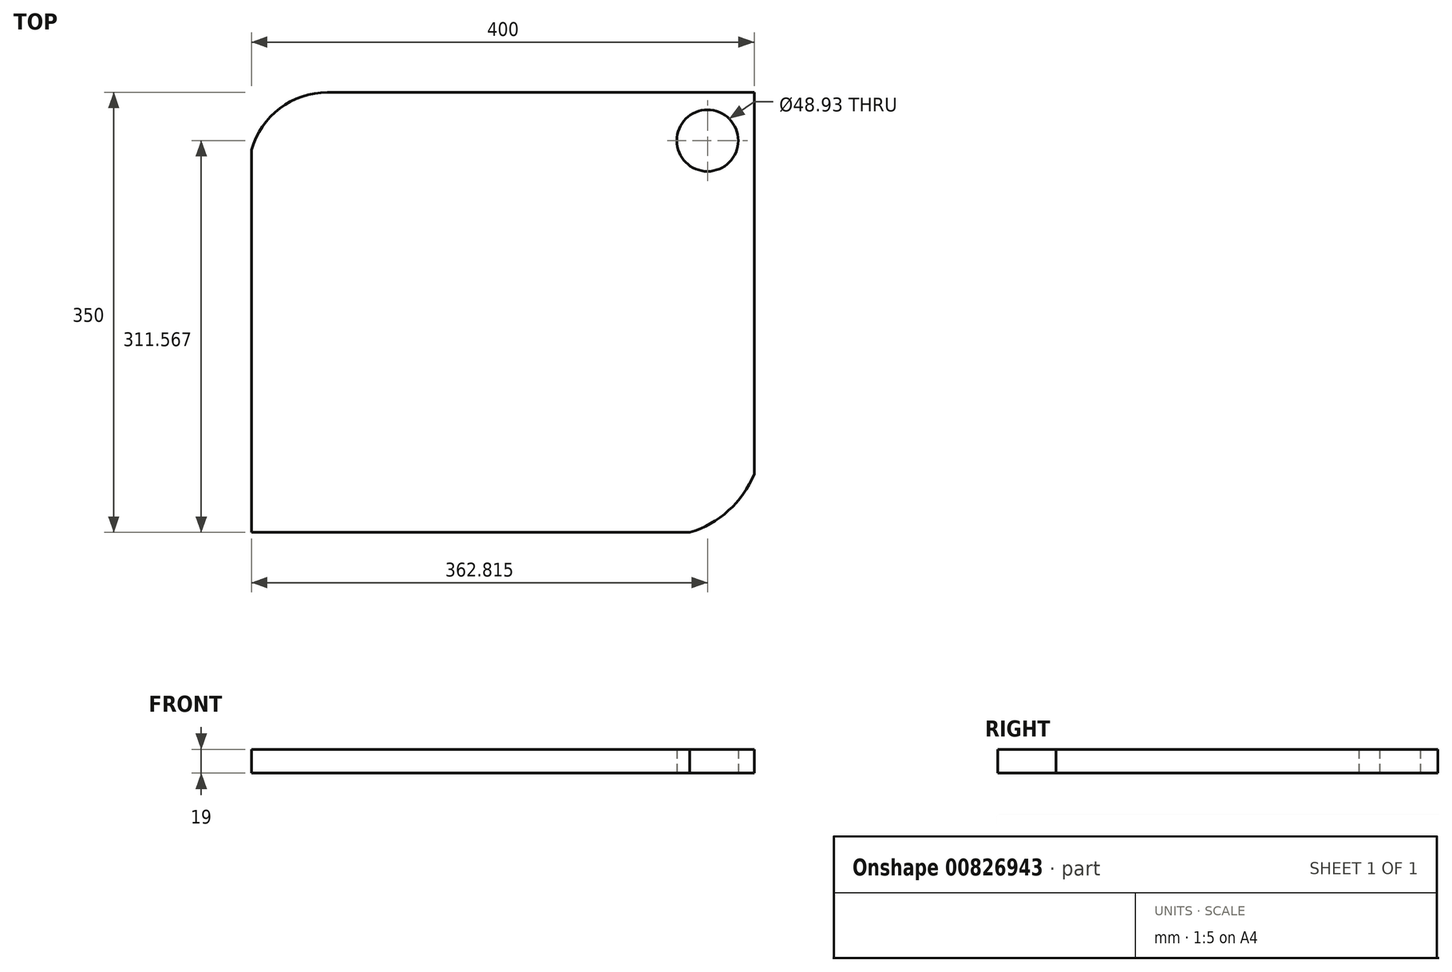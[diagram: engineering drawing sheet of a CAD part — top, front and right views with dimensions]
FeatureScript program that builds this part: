
annotation { "Feature Type Name" : "Feature", "Feature Type Description" : "" }
export const myFeature = defineFeature(function(context is Context, id is Id, definition is map)
    precondition{}
    {
        {
            var Q0;
            Q0=qCreatedBy(makeId("Top.planeOp"),FACE);
            var sketch = newSketch(context, id + "F0", { "sketchPlane" : qUnion([Q0])});
            skLineSegment(sketch, "E0.bottom", {"start": v(200, -175) * mm, "end": v(-200, -175) * mm});
            skLineSegment(sketch, "E0.top", {"start": v(200, 175) * mm, "end": v(-200, 175) * mm});
            skLineSegment(sketch, "E0.left", {"start": v(200, -175) * mm, "end": v(200, 175) * mm});
            skLineSegment(sketch, "E0.right", {"start": v(-200, -175) * mm, "end": v(-200, 175) * mm});
            skPoint(sketch, "E0.middle", {"position": v(0, 0) * mm});
            skSolve(sketch);
        }
        {
            var Q0;
            Q0=qSketchRegion(id+"F0",true);
            extrude(context, id + "F1", {"entities" : qUnion([Q0]), "depth" : 19 * mm, "offsetDistance" : 25 * mm});
        }
        {
            var Q0;
            Q0=makeQuery(id+"F1.opExtrude","CAP_FACE",FACE,{"disambiguationData":[OSD([sQuery(id+"F0.wireOp",EDGE,"E0.bottom"),sQuery(id+"F0.wireOp",EDGE,"E0.top"),sQuery(id+"F0.wireOp",EDGE,"E0.left"),sQuery(id+"F0.wireOp",EDGE,"E0.right")])],"isStart":false});
            var sketch = newSketch(context, id + "F2", { "sketchPlane" : qUnion([Q0])});
            skArc(sketch, "E1", {"start": v(-139.55, 175) * mm, "mid": v(-177.47, 162.18) * mm, "end": v(-200, 129.1) * mm});
            skSolve(sketch);
        }
        {
            var Q0;
            Q0 = qSketchRegion(id + "F2", true);
            var Q1;
            {var subQ0=sQuery(id+"F2.wireOp",EDGE,"E1");Q1=makeQuery(id+"F2.imprint","IMPRINT",FACE,{"disambiguationData":[TD([[makeQuery(id+"F2.imprint","IMPRINT",EDGE,{"derivedFrom":subQ0}),-1.0]])]});}
            extrude(context, id + "F3", {"entities" : qUnion([Q0, Q1]), "operationType" : NewBodyOperationType.REMOVE, "endBound" : BoundingType.THROUGH_ALL, "oppositeDirection" : true, "depth" : 25 * mm, "offsetDistance" : 25 * mm});
        }
        {
            var Q0;
            Q0=makeQuery(id+"F1.opExtrude","CAP_FACE",FACE,{"disambiguationData":[OSD([sQuery(id+"F0.wireOp",EDGE,"E0.bottom"),sQuery(id+"F0.wireOp",EDGE,"E0.top"),sQuery(id+"F0.wireOp",EDGE,"E0.left"),sQuery(id+"F0.wireOp",EDGE,"E0.right")])],"isStart":false});
            var sketch = newSketch(context, id + "F4", { "sketchPlane" : qUnion([Q0])});
            skArc(sketch, "E2", {"start": v(148.7, -175) * mm, "mid": v(179.6, -157.64) * mm, "end": v(200, -128.67) * mm});
            skSolve(sketch);
        }
        {
            var Q0;
            Q0 = qSketchRegion(id + "F4", true);
            var Q1;
            {var subQ0=sQuery(id+"F4.wireOp",EDGE,"E2");Q1=makeQuery(id+"F4.imprint","IMPRINT",FACE,{"disambiguationData":[TD([[makeQuery(id+"F4.imprint","IMPRINT",EDGE,{"derivedFrom":subQ0}),-1.0]])]});}
            extrude(context, id + "F5", {"entities" : qUnion([Q0, Q1]), "operationType" : NewBodyOperationType.REMOVE, "endBound" : BoundingType.THROUGH_ALL, "oppositeDirection" : true, "depth" : 25 * mm, "offsetDistance" : 25 * mm});
        }
        {
            var Q0;
            Q0=makeQuery(id+"F1.opExtrude","CAP_FACE",FACE,{"disambiguationData":[OSD([sQuery(id+"F0.wireOp",EDGE,"E0.bottom"),sQuery(id+"F0.wireOp",EDGE,"E0.top"),sQuery(id+"F0.wireOp",EDGE,"E0.left"),sQuery(id+"F0.wireOp",EDGE,"E0.right")])],"isStart":true});
            var sketch = newSketch(context, id + "F6", { "sketchPlane" : qUnion([Q0])});
            skCircle(sketch, "E3", {"center": v(162.82, -136.57) * mm, "radius": 24.47 * mm});
            skPoint(sketch, "E3.first.point", {"position": v(142.17, -123.44) * mm});
            skPoint(sketch, "E3.second.point", {"position": v(182.66, -150.88) * mm});
            skPoint(sketch, "E3.third.point", {"position": v(176.13, -116.04) * mm});
            skSolve(sketch);
        }
        {
            var Q0;
            Q0=makeQuery(id+"F6.imprint","IMPRINT",FACE,{"disambiguationData":[TD([[makeQuery(id+"F6.imprint","IMPRINT",EDGE,{"derivedFrom":sQuery(id+"F6.wireOp",EDGE,"E3")}),1.0]])]});
            extrude(context, id + "F7", {"entities" : qUnion([Q0]), "operationType" : NewBodyOperationType.REMOVE, "endBound" : BoundingType.THROUGH_ALL, "oppositeDirection" : true, "depth" : 25 * mm, "offsetDistance" : 25 * mm});
        }
    });
